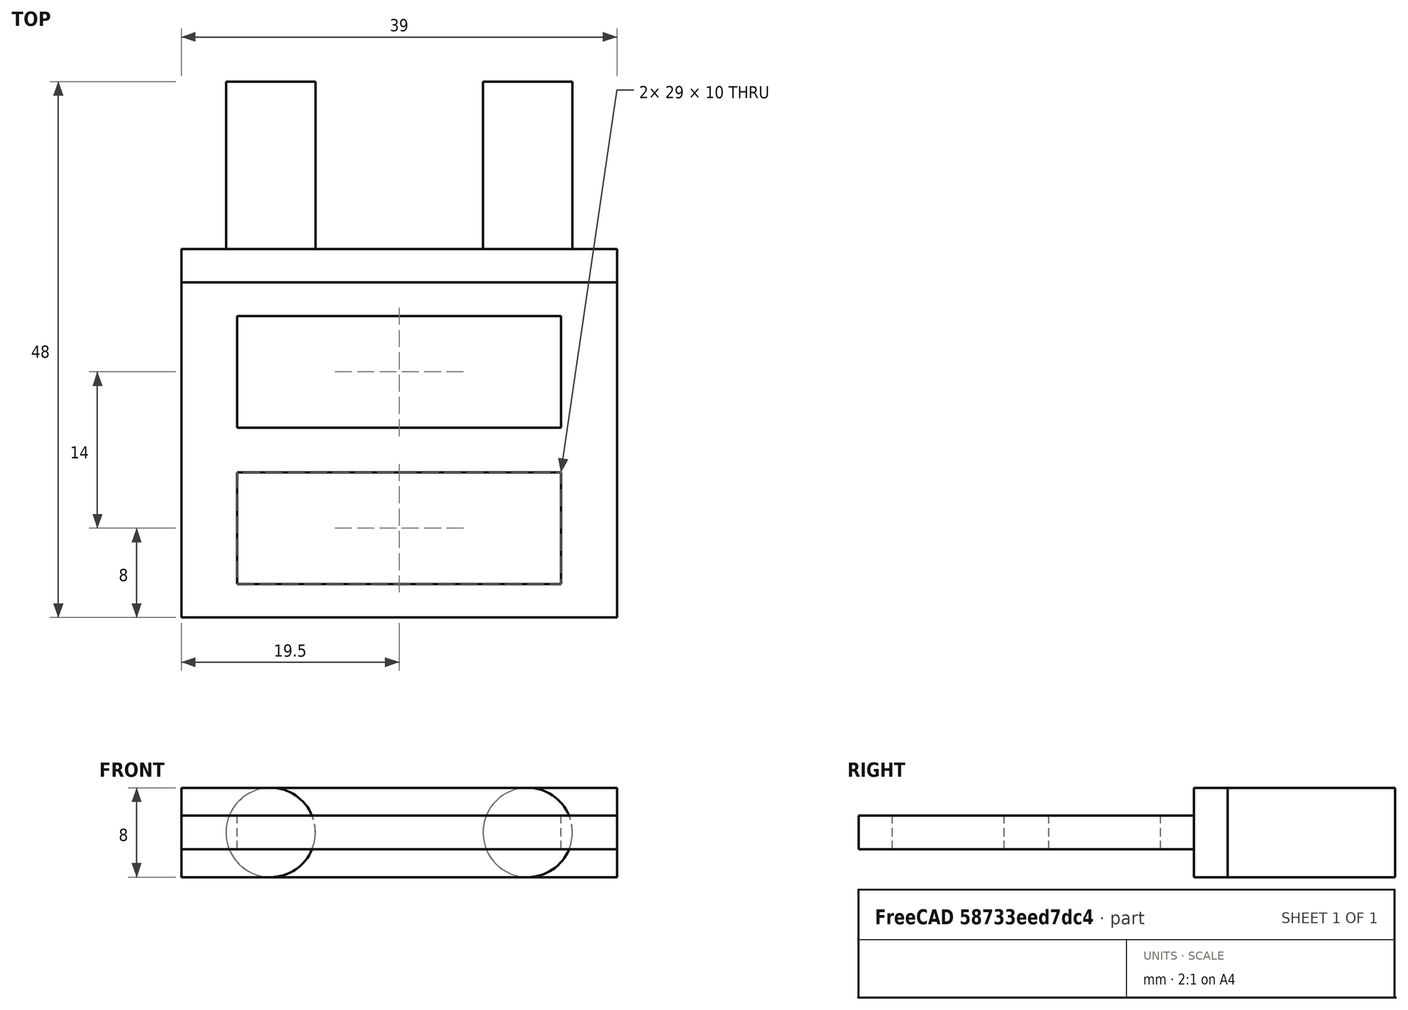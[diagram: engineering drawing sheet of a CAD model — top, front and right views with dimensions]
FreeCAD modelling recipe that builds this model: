
FCSTD DOCUMENT  (FreeCAD 0.15R4671 (Git))
Label: Holder_V1
License: All rights reserved
LicenseURL: http://en.wikipedia.org/wiki/All_rights_reserved
objects: Part::Box×4, Part::Cylinder×2, Part::MultiFuse×1, Part::Cut×1
note: 8 computed .brp shape members not serialized (recipe doc carries the construction recipe); baked Part::Feature solids carry a one-line shape summary decoded from their .brp

FEATURE [Part::Box] Box  label="Base"
  Height = 8
  Length = 39
  Placement = pos=(-8,-18,-4) rot=(0,0,1;0rad)
  Width = 3
FEATURE [Part::Cylinder] Cylinder  label="Pin2"
  Angle = 360
  Height = 15
  Placement = pos=(23,0,0) rot=(1,0,0;1.5708rad)
  Radius = 4
FEATURE [Part::Cylinder] Cylinder001  label="Pin1"
  Angle = 360
  Height = 15
  Placement = pos=(0,0,0) rot=(1,0,0;1.5708rad)
  Radius = 4
FEATURE [Part::Box] Box001  label="Holder"
  Height = 3
  Length = 39
  Placement = pos=(-8,-48,-1.5) rot=(0,0,1;0rad)
  Width = 30
FEATURE [Part::Box] Box002  label="Cut1"
  Height = 3
  Length = 29
  Placement = pos=(-3,-31,-1.5) rot=(0,0,1;0rad)
  Width = 10
FEATURE [Part::Box] Box003  label="Cut2"
  Height = 3
  Length = 29
  Placement = pos=(-3,-45,-1.5) rot=(0,0,1;0rad)
  Width = 10
FEATURE [Part::MultiFuse] Fusion
  Shapes = -> [Box002,Box003]
FEATURE [Part::Cut] Cut
  Base = -> Box001
  Tool = -> Fusion
